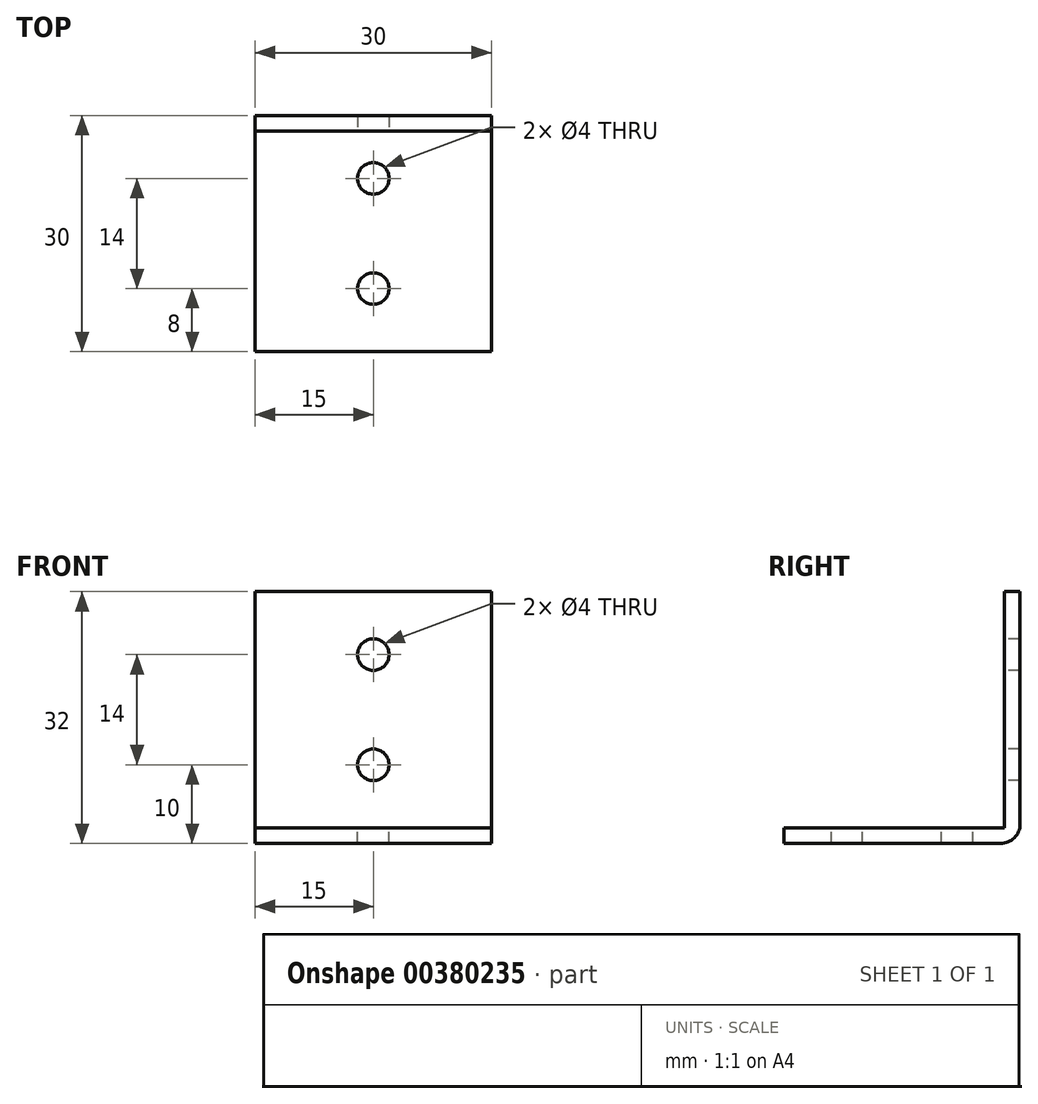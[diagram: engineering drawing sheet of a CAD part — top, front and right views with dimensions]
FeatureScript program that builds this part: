
annotation { "Feature Type Name" : "Feature", "Feature Type Description" : "" }
export const myFeature = defineFeature(function(context is Context, id is Id, definition is map)
    precondition{}
    {
        {
            var Q0;
            Q0=qCreatedBy(makeId("Top.planeOp"),FACE);
            var sketch = newSketch(context, id + "F0", { "sketchPlane" : qUnion([Q0])});
            skLineSegment(sketch, "E0.bottom", {"start": v(15, -15) * mm, "end": v(-15, -15) * mm});
            skLineSegment(sketch, "E0.top", {"start": v(15, 15) * mm, "end": v(-15, 15) * mm});
            skLineSegment(sketch, "E0.left", {"start": v(15, -15) * mm, "end": v(15, 15) * mm});
            skLineSegment(sketch, "E0.right", {"start": v(-15, -15) * mm, "end": v(-15, 15) * mm});
            skPoint(sketch, "E0.middle", {"position": v(0, 0) * mm});
            skSolve(sketch);
        }
        {
            var Q0;
            Q0=makeQuery(id+"F0.imprint","IMPRINT",FACE,{"disambiguationData":[TD([[makeQuery(id+"F0.imprint","IMPRINT",EDGE,{"derivedFrom":sQuery(id+"F0.wireOp",EDGE,"E0.bottom")}),-1.0]])]});
            extrude(context, id + "F1", {"entities" : qUnion([Q0]), "depth" : 2 * mm});
        }
        {
            var Q0;
            Q0=makeQuery(id+"F1.opExtrude","CAP_FACE",FACE,{"disambiguationData":[OSD([sQuery(id+"F0.wireOp",EDGE,"E0.bottom"),sQuery(id+"F0.wireOp",EDGE,"E0.top"),sQuery(id+"F0.wireOp",EDGE,"E0.left"),sQuery(id+"F0.wireOp",EDGE,"E0.right")])],"isStart":false});
            var sketch = newSketch(context, id + "F2", { "sketchPlane" : qUnion([Q0])});
            skLineSegment(sketch, "E1", {"start": v(0, -15) * mm, "end": v(0, 15) * mm, "construction": true});
            skLineSegment(sketch, "E2", {"start": v(0, 15) * mm, "end": v(0, 7) * mm, "construction": true});
            skLineSegment(sketch, "E3", {"start": v(0, -15) * mm, "end": v(0, -7) * mm, "construction": true});
            skLineSegment(sketch, "E4", {"start": v(0, -7) * mm, "end": v(0, -15) * mm, "construction": true});
            skCircle(sketch, "E5", {"center": v(0, 7) * mm, "radius": 2 * mm});
            skCircle(sketch, "E6", {"center": v(0, -7) * mm, "radius": 2 * mm});
            skLineSegment(sketch, "E7.bottom", {"start": v(-15, 15) * mm, "end": v(15, 15) * mm});
            skLineSegment(sketch, "E7.top", {"start": v(-15, 13) * mm, "end": v(15, 13) * mm});
            skLineSegment(sketch, "E7.left", {"start": v(-15, 15) * mm, "end": v(-15, 13) * mm});
            skLineSegment(sketch, "E7.right", {"start": v(15, 15) * mm, "end": v(15, 13) * mm});
            skSolve(sketch);
        }
        {
            var Q0;
            Q0=makeQuery(id+"F2.imprint","IMPRINT",FACE,{"disambiguationData":[TD([[makeQuery(id+"F2.imprint","IMPRINT",EDGE,{"derivedFrom":sQuery(id+"F2.wireOp",EDGE,"E5")}),1.0]])]});
            var Q1;
            Q1=makeQuery(id+"F2.imprint","IMPRINT",FACE,{"disambiguationData":[TD([[makeQuery(id+"F2.imprint","IMPRINT",EDGE,{"derivedFrom":sQuery(id+"F2.wireOp",EDGE,"E6")}),1.0]])]});
            extrude(context, id + "F3", {"entities" : qUnion([Q0, Q1]), "operationType" : NewBodyOperationType.REMOVE, "oppositeDirection" : true, "depth" : 25 * mm});
        }
        {
            var Q0;
            Q0=makeQuery(id+"F2.imprint","IMPRINT",FACE,{"disambiguationData":[TD([[makeQuery(id+"F2.imprint","IMPRINT",EDGE,{"derivedFrom":sQuery(id+"F2.wireOp",EDGE,"E7.bottom")}),1.0]])]});
            extrude(context, id + "F4", {"entities" : qUnion([Q0]), "operationType" : NewBodyOperationType.ADD, "depth" : 30 * mm});
        }
        {
            var Q0;
            Q0=makeQuery(id+"F4.opExtrude","SWEPT_FACE",FACE,{"disambiguationData":[OSD([sQuery(id+"F2.wireOp",EDGE,"E7.top")])]});
            var sketch = newSketch(context, id + "F5", { "sketchPlane" : qUnion([Q0])});
            skLineSegment(sketch, "E8", {"start": v(0, 32) * mm, "end": v(0, 2) * mm, "construction": true});
            skLineSegment(sketch, "E9", {"start": v(0, 2) * mm, "end": v(0, 32) * mm, "construction": true});
            skLineSegment(sketch, "E10", {"start": v(0, 24) * mm, "end": v(0, 32) * mm, "construction": true});
            skLineSegment(sketch, "E11", {"start": v(0, 2) * mm, "end": v(0, 10) * mm, "construction": true});
            skCircle(sketch, "E12", {"center": v(0, 24) * mm, "radius": 2 * mm});
            skCircle(sketch, "E13", {"center": v(0, 10) * mm, "radius": 2 * mm});
            skSolve(sketch);
        }
        {
            var Q0;
            Q0=makeQuery(id+"F5.imprint","IMPRINT",FACE,{"disambiguationData":[TD([[makeQuery(id+"F5.imprint","IMPRINT",EDGE,{"derivedFrom":sQuery(id+"F5.wireOp",EDGE,"E12")}),1.0]])]});
            var Q1;
            Q1=makeQuery(id+"F5.imprint","IMPRINT",FACE,{"disambiguationData":[TD([[makeQuery(id+"F5.imprint","IMPRINT",EDGE,{"derivedFrom":sQuery(id+"F5.wireOp",EDGE,"E13")}),1.0]])]});
            extrude(context, id + "F6", {"entities" : qUnion([Q0, Q1]), "operationType" : NewBodyOperationType.REMOVE, "oppositeDirection" : true, "depth" : 25 * mm});
        }
        {
            var Q0;
            Q0=makeQuery(id+"F1.opExtrude","CAP_EDGE",EDGE,{"disambiguationData":[OSD([sQuery(id+"F0.wireOp",EDGE,"E0.top")])],"isStart":true});
            fillet(context, id + "F7", {"entities" : qUnion([Q0]), "radius" : 2.5 * mm, "tangentPropagation" : true, "allowEdgeOverflow" : false});
        }
    });
